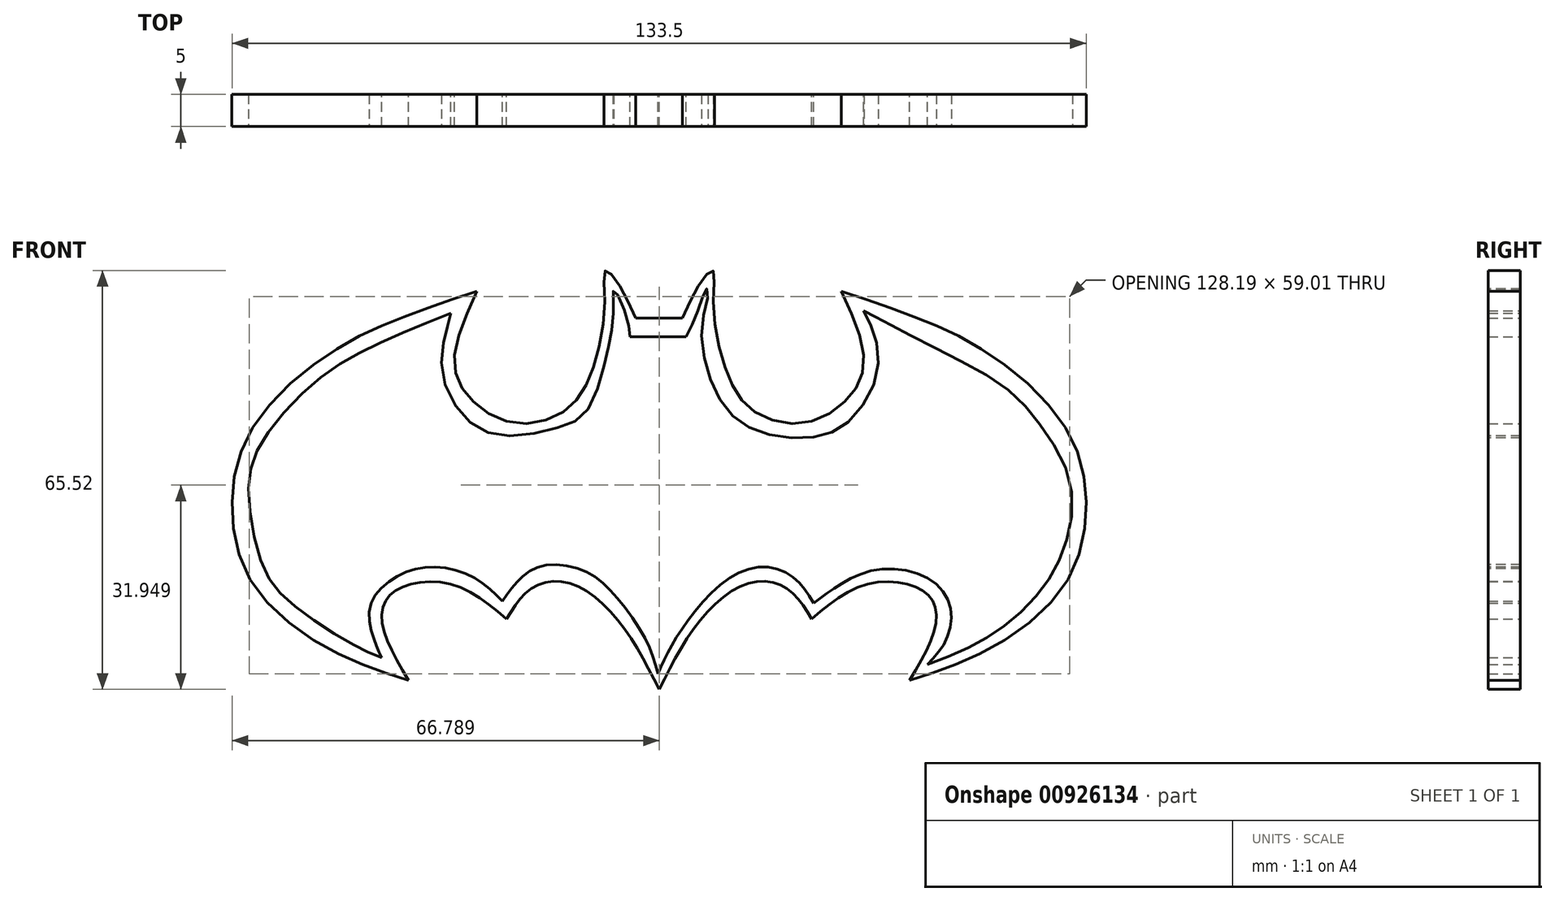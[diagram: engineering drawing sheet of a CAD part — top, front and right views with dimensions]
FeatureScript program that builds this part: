
annotation { "Feature Type Name" : "Feature", "Feature Type Description" : "" }
export const myFeature = defineFeature(function(context is Context, id is Id, definition is map)
    precondition{}
    {
        {
            var Q0;
            Q0=qCreatedBy(makeId("Front.planeOp"),FACE);
            var sketch = newSketch(context, id + "F0", { "sketchPlane" : qUnion([Q0])});
            skFitSpline(sketch, "E0", {"points": [v(-11.88, 40.08) * mm, v(-15, 46.1) * mm, v(-16.6, 47.51) * mm, v(-16.7, 42.19) * mm, v(-18.81, 31.54) * mm, v(-22.83, 25.61) * mm, v(-30.97, 23.7) * mm, v(-37.9, 27.72) * mm, v(-40.22, 33.65) * mm, v(-36.7, 44.3) * mm], "startDerivative": vector(-27.47, 61.17) * mm, "endDerivative": vector(36.86, 81.26) * mm});
            skFitSpline(sketch, "E1", {"points": [v(-36.7, 44.3) * mm, v(-48.62, 40.08) * mm, v(-59.47, 34.7) * mm, v(-71.4, 23.5) * mm, v(-74.96, 11.2) * mm, v(-71.4, -1.96) * mm, v(-58.58, -12.28) * mm, v(-47.37, -16.56) * mm], "startDerivative": vector(-88.82, -30.07) * mm, "endDerivative": vector(81.02, -25.32) * mm});
            skFitSpline(sketch, "E2", {"points": [v(-47.37, -16.56) * mm, v(-51.29, -8.55) * mm, v(-50.93, -4.1) * mm, v(-47.37, -1.6) * mm, v(-39.9, -1.78) * mm, v(-32.06, -6.95) * mm], "startDerivative": vector(-21.59, 36.38) * mm, "endDerivative": vector(31.76, -26.69) * mm});
            skFitSpline(sketch, "E3", {"points": [v(-32.06, -6.95) * mm, v(-28.33, -2.32) * mm, v(-22.63, -1.25) * mm, v(-14.8, -6.95) * mm, v(-8.21, -17.98) * mm], "startDerivative": vector(15.34, 24.96) * mm, "endDerivative": vector(19, -37.78) * mm});
            skLineSegment(sketch, "E4", {"start": v(-8.21, 40.08) * mm, "end": v(-11.88, 40.08) * mm});
            skLineSegment(sketch, "E5", {"start": v(-8.21, 40.08) * mm, "end": v(-8.21, -17.98) * mm, "construction": true});
            skLineSegment(sketch, "E6.MirrorCS", {"start": v(-8.21, 40.08) * mm, "end": v(-4.54, 40.08) * mm});
            skFitSpline(sketch, "E7.MirrorCS", {"points": [v(-4.54, 40.08) * mm, v(-1.43, 46.1) * mm, v(0.18, 47.51) * mm, v(0.28, 42.19) * mm, v(2.4, 31.54) * mm, v(6.4, 25.61) * mm, v(14.55, 23.7) * mm, v(21.48, 27.72) * mm, v(23.8, 33.65) * mm, v(20.27, 44.3) * mm], "startDerivative": vector(27.47, 61.17) * mm, "endDerivative": vector(-36.86, 81.26) * mm});
            skFitSpline(sketch, "E8.MirrorCS", {"points": [v(20.27, 44.3) * mm, v(32.2, 40.08) * mm, v(43.05, 34.7) * mm, v(54.97, 23.5) * mm, v(58.53, 11.2) * mm, v(54.97, -1.96) * mm, v(42.16, -12.28) * mm, v(30.95, -16.56) * mm], "startDerivative": vector(88.82, -30.07) * mm, "endDerivative": vector(-81.02, -25.32) * mm});
            skFitSpline(sketch, "E9.MirrorCS", {"points": [v(30.95, -16.56) * mm, v(34.86, -8.55) * mm, v(34.5, -4.1) * mm, v(30.95, -1.6) * mm, v(23.47, -1.78) * mm, v(15.64, -6.95) * mm], "startDerivative": vector(21.59, 36.38) * mm, "endDerivative": vector(-31.76, -26.69) * mm});
            skFitSpline(sketch, "E10.MirrorCS", {"points": [v(15.64, -6.95) * mm, v(11.9, -2.32) * mm, v(6.2, -1.25) * mm, v(-1.63, -6.95) * mm, v(-8.21, -17.98) * mm], "startDerivative": vector(-15.34, 24.96) * mm, "endDerivative": vector(-19, -37.78) * mm});
            skFitSpline(sketch, "E11", {"points": [v(-40.78, 40.85) * mm, v(-52.94, 35.7) * mm, v(-62.13, 29.96) * mm, v(-70.48, 20.34) * mm, v(-72.36, 12.84) * mm, v(-70, 1.01) * mm, v(-65.47, -4.67) * mm, v(-56.26, -10.86) * mm, v(-51.58, -13.02) * mm], "startDerivative": vector(-87.62, -35) * mm, "endDerivative": vector(46.21, -18.6) * mm});
            skFitSpline(sketch, "E12", {"points": [v(-51.58, -13.02) * mm, v(-52.73, -10.21) * mm, v(-53.38, -4.96) * mm, v(-49.6, -0.57) * mm, v(-43.57, 1.18) * mm, v(-36.85, -0.66) * mm, v(-32.7, -4.2) * mm], "startDerivative": vector(-9.03, 20.06) * mm, "endDerivative": vector(21.98, -22.96) * mm});
            skFitSpline(sketch, "E13", {"points": [v(-32.7, -4.2) * mm, v(-30.27, -1) * mm, v(-26.5, 1.35) * mm, v(-20.17, 0.67) * mm, v(-15.25, -3.14) * mm, v(-10.23, -10.34) * mm, v(-8.41, -15.54) * mm], "startDerivative": vector(16.19, 23.86) * mm, "endDerivative": vector(8.1, -30.56) * mm});
            skFitSpline(sketch, "E14", {"points": [v(-8.41, -15.54) * mm, v(-6.77, -12.05) * mm, v(-3.6, -7.05) * mm, v(2.69, -0.62) * mm, v(8.87, 1.14) * mm, v(13.37, -0.98) * mm, v(15.92, -4.47) * mm], "startDerivative": vector(10.93, 24.64) * mm, "endDerivative": vector(15.02, -25.38) * mm});
            skFitSpline(sketch, "E15", {"points": [v(15.92, -4.47) * mm, v(19.52, -1.95) * mm, v(25.78, 0.75) * mm, v(33.87, -0.66) * mm, v(37.33, -5.16) * mm, v(36.5, -10.52) * mm, v(33.7, -14.08) * mm], "startDerivative": vector(23.02, 16.87) * mm, "endDerivative": vector(-21.14, -21.62) * mm});
            skFitSpline(sketch, "E16", {"points": [v(33.7, -14.08) * mm, v(40.78, -11.13) * mm, v(46.79, -7.18) * mm, v(52.01, -1.75) * mm, v(55.3, 4.92) * mm, v(56.12, 14.03) * mm, v(51.57, 23.1) * mm, v(45.58, 29.42) * mm, v(34.11, 35.8) * mm, v(26.63, 39.72) * mm, v(23.73, 41.25) * mm], "startDerivative": vector(74.78, 27.94) * mm, "endDerivative": vector(-41.1, 21.48) * mm});
            skFitSpline(sketch, "E17", {"points": [v(23.73, 41.25) * mm, v(25.62, 36.93) * mm, v(25.56, 30.31) * mm, v(21.09, 23.65) * mm, v(15.92, 21.46) * mm, v(8.17, 22.07) * mm, v(2.62, 25.48) * mm, v(-0.74, 32.2) * mm, v(-1.45, 39.52) * mm, v(-0.58, 44.05) * mm, v(-0.82, 44.68) * mm, v(-1.43, 43.32) * mm, v(-2.7, 39.84) * mm, v(-4, 37.15) * mm], "startDerivative": vector(28.4, -53.07) * mm, "endDerivative": vector(-21.87, -42.24) * mm});
            skFitSpline(sketch, "E18", {"points": [v(-4, 37.15) * mm, v(-12.77, 37.15) * mm], "startDerivative": vector(-8.77, 0) * mm, "endDerivative": vector(-8.77, 0) * mm});
            skFitSpline(sketch, "E19", {"points": [v(-12.77, 37.15) * mm, v(-13.05, 39.24) * mm, v(-14.53, 43.42) * mm, v(-15.3, 44.43) * mm, v(-15.4, 43.77) * mm, v(-15.32, 42.14) * mm, v(-15.65, 38.04) * mm, v(-16.7, 33.13) * mm, v(-19.52, 25.55) * mm, v(-23.75, 23.01) * mm, v(-32.59, 21.68) * mm, v(-38.58, 24.52) * mm, v(-42.14, 31.84) * mm, v(-41.5, 37.82) * mm, v(-40.78, 40.85) * mm], "startDerivative": vector(-2.58, 36.51) * mm, "endDerivative": vector(10.78, 45.38) * mm});
            skSolve(sketch);
        }
        {
            var Q0;
            Q0 = qSketchRegion(id + "F0", true);
            extrude(context, id + "F1", {"entities" : qUnion([Q0]), "depth" : 5 * mm, "offsetDistance" : 25 * mm});
        }
    });
